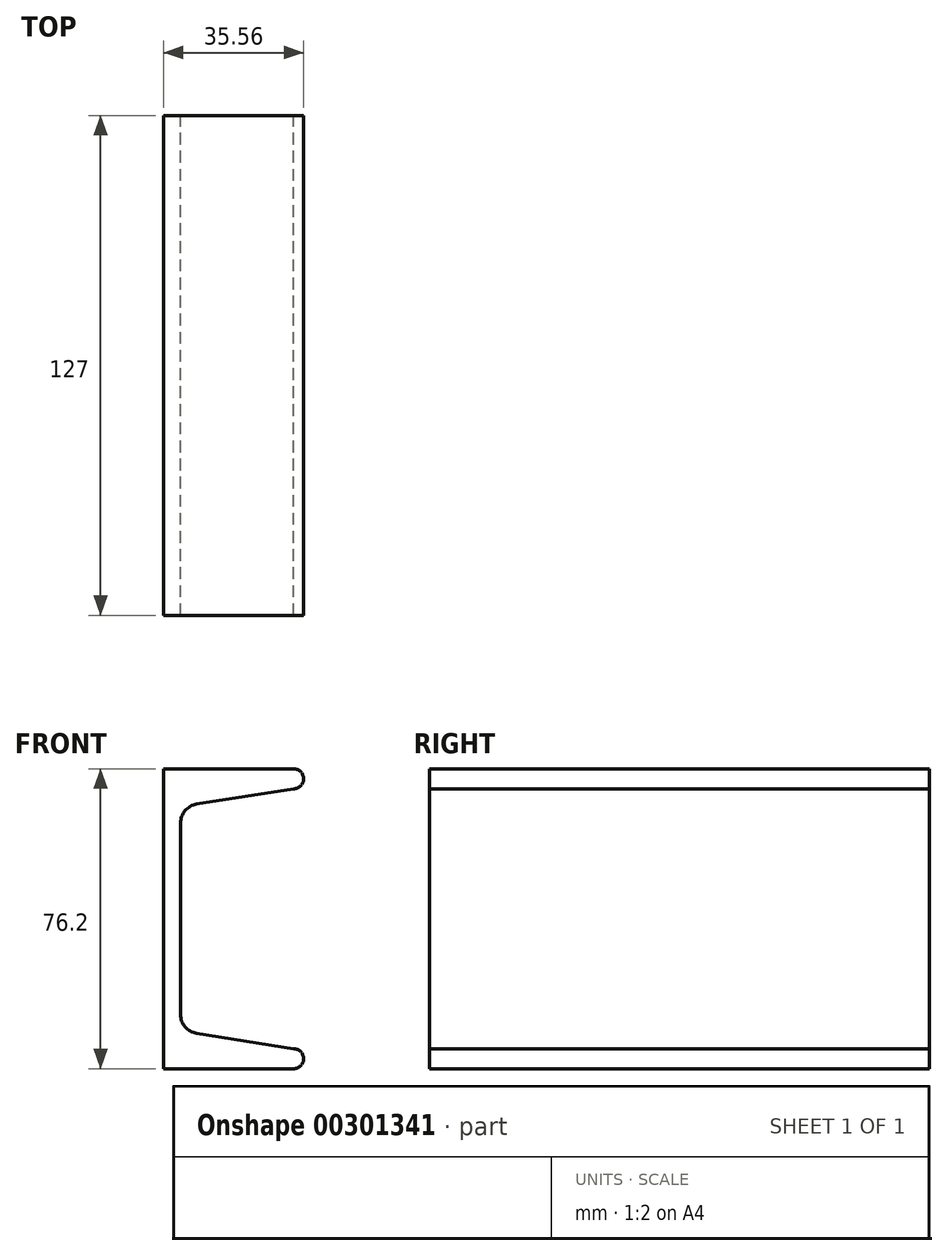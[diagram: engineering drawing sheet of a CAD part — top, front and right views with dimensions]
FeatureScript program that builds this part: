
annotation { "Feature Type Name" : "Feature", "Feature Type Description" : "" }
export const myFeature = defineFeature(function(context is Context, id is Id, definition is map)
    precondition{}
    {
        {
            var Q0;
            Q0=qCreatedBy(makeId("Front.planeOp"),FACE);
            var sketch = newSketch(context, id + "F0", { "sketchPlane" : qUnion([Q0])});
            skLineSegment(sketch, "E0", {"start": v(0, 0) * mm, "end": v(0, 38.1) * mm});
            skLineSegment(sketch, "E1", {"start": v(0, 38.1) * mm, "end": v(33.02, 38.1) * mm});
            skArc(sketch, "E2", {"start": v(33.02, 33.02) * mm, "mid": v(35.56, 35.56) * mm, "end": v(33.02, 38.1) * mm});
            skLineSegment(sketch, "E3", {"start": v(33.02, 33.02) * mm, "end": v(8.41, 29.12) * mm});
            skLineSegment(sketch, "E4", {"start": v(4.32, 24.33) * mm, "end": v(4.32, 0) * mm});
            skLineSegment(sketch, "E5.MirrorCS", {"start": v(33.02, -33.02) * mm, "end": v(8.41, -29.12) * mm});
            skLineSegment(sketch, "E6.MirrorCS", {"start": v(0, 0) * mm, "end": v(0, -38.1) * mm});
            skLineSegment(sketch, "E7.MirrorCS", {"start": v(4.32, -24.33) * mm, "end": v(4.32, 0) * mm});
            skLineSegment(sketch, "E8.MirrorCS", {"start": v(0, -38.1) * mm, "end": v(33.02, -38.1) * mm});
            skArc(sketch, "E9.MirrorCS", {"start": v(33.02, -33.02) * mm, "mid": v(35.56, -35.56) * mm, "end": v(33.02, -38.1) * mm});
            skPoint(sketch, "E10.visualSharp", {"position": v(4.32, 28.47) * mm});
            skArc(sketch, "E10.filletArc", {"start": v(8.41, 29.12) * mm, "mid": v(5.48, 27.48) * mm, "end": v(4.32, 24.33) * mm});
            skPoint(sketch, "E11.visualSharp", {"position": v(4.32, -28.47) * mm});
            skArc(sketch, "E11.filletArc", {"start": v(4.32, -24.33) * mm, "mid": v(5.48, -27.48) * mm, "end": v(8.41, -29.12) * mm});
            skSolve(sketch);
        }
        {
            var Q0;
            Q0=makeQuery(id+"F0.imprint","IMPRINT",FACE,{"disambiguationData":[TD([[makeQuery(id+"F0.imprint","IMPRINT",EDGE,{"derivedFrom":sQuery(id+"F0.wireOp",EDGE,"E0")}),-1.0]])]});
            extrude(context, id + "F1", {"entities" : qUnion([Q0]), "depth" : 127 * mm});
        }
    });
